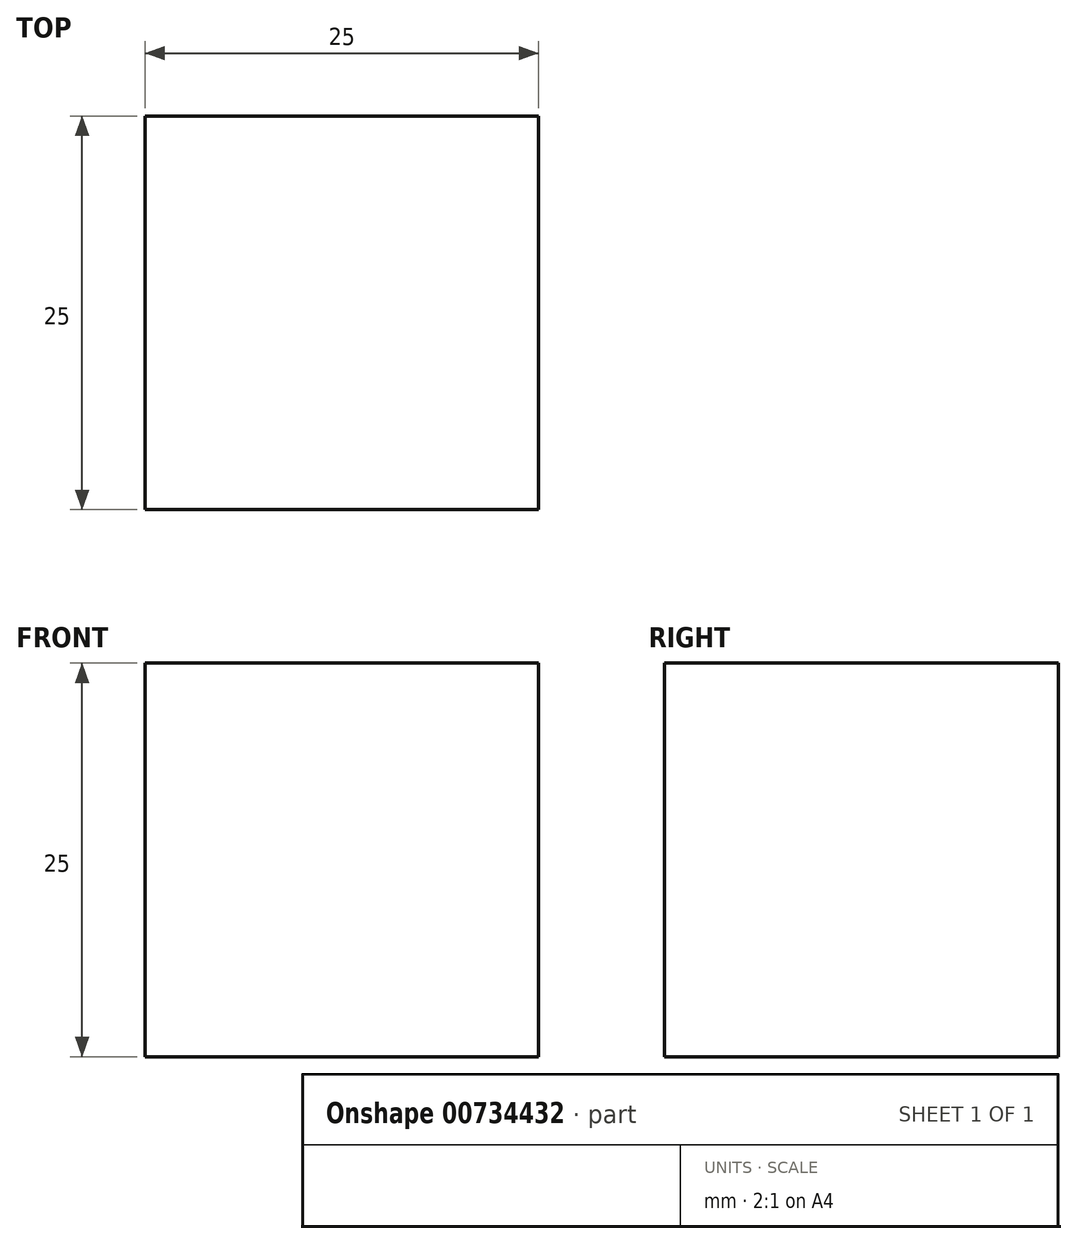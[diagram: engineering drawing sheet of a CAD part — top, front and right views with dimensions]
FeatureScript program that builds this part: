
annotation { "Feature Type Name" : "Feature", "Feature Type Description" : "" }
export const myFeature = defineFeature(function(context is Context, id is Id, definition is map)
    precondition{}
    {
        {
            var Q0;
            Q0=qCreatedBy(makeId("Top.planeOp"),FACE);
            var sketch = newSketch(context, id + "F0", { "sketchPlane" : qUnion([Q0])});
            skLineSegment(sketch, "E0.bottom", {"start": v(-12.5, -12.5) * mm, "end": v(12.5, -12.5) * mm});
            skLineSegment(sketch, "E0.top", {"start": v(-12.5, 12.5) * mm, "end": v(12.5, 12.5) * mm});
            skLineSegment(sketch, "E0.left", {"start": v(-12.5, -12.5) * mm, "end": v(-12.5, 12.5) * mm});
            skLineSegment(sketch, "E0.right", {"start": v(12.5, -12.5) * mm, "end": v(12.5, 12.5) * mm});
            skPoint(sketch, "E0.middle", {"position": v(0, 0) * mm});
            skSolve(sketch);
        }
        {
            var Q0;
            Q0=makeQuery(id+"F0.imprint","IMPRINT",FACE,{"disambiguationData":[TD([[makeQuery(id+"F0.imprint","IMPRINT",EDGE,{"derivedFrom":sQuery(id+"F0.wireOp",EDGE,"E0.bottom")}),1.0]])]});
            extrude(context, id + "F1", {"entities" : qUnion([Q0]), "depth" : 25 * mm, "offsetDistance" : 25 * mm});
        }
    });
